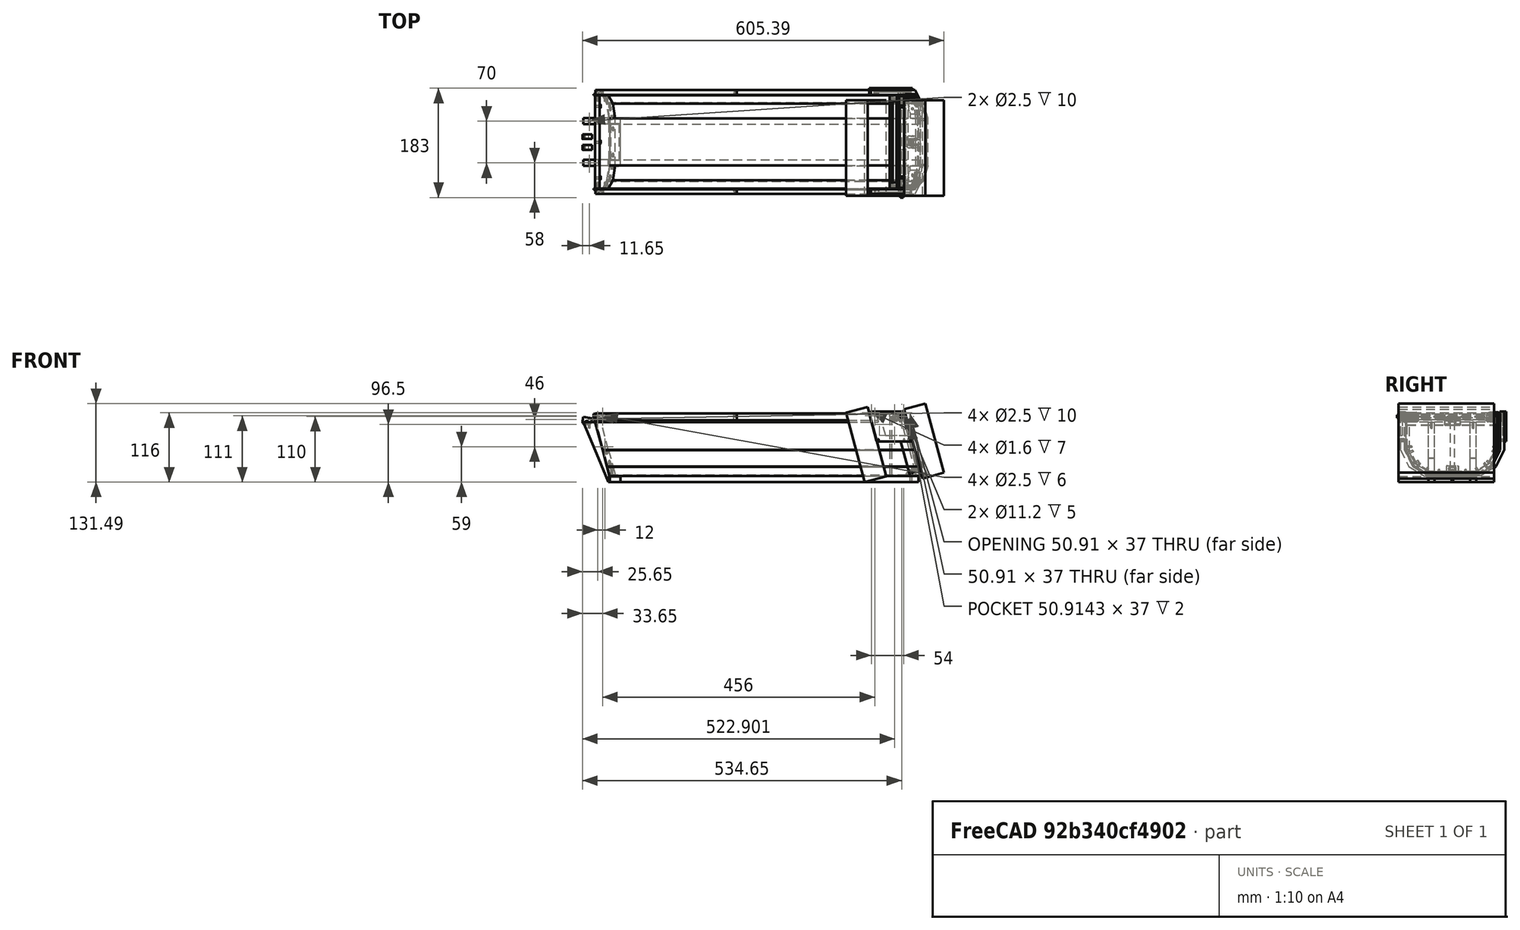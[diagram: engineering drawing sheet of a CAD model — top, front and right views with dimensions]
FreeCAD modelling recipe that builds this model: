
FCSTD DOCUMENT  (FreeCAD 0.16R)
Label: kipper
License: CC-BY 3.0
LicenseURL: http://creativecommons.org/licenses/by/3.0/
objects: Part::Cylinder×116, Part::Box×102, Part::MultiFuse×101, Part::Cut×98, Part::Fillet×19, Part::Extrusion×13, Part::Chamfer×12, Part::Feature×11, Part::Mirroring×6, Sketcher::SketchObject×5, Part::RegularPolygon×1, App::DocumentObjectGroup×1
note: 484 computed .brp shape members not serialized (recipe doc carries the construction recipe); baked Part::Feature solids carry a one-line shape summary decoded from their .brp

FEATURE [Part::Box] Box
  Height = 2
  Length = 560
  Width = 80
FEATURE [Part::Box] Box001
  Height = 2
  Length = 560
  Placement = pos=(0,80,0) rot=(1,0,0;0.541051rad)
  Width = 30
FEATURE [Part::Box] Box002
  Height = 2
  Length = 560
  Placement = pos=(0,106,16) rot=(1,0,0;1.09956rad)
  Width = 31
FEATURE [Part::Box] Box003
  Height = 2
  Length = 560
  Placement = pos=(0,120,44) rot=(1,0,0;1.5708rad)
  Width = 60
FEATURE [Part::Box] Box004
  Height = 2
  Length = 560
  Placement = pos=(0,120,44) rot=(1,0,0;1.5708rad)
  Width = 60
FEATURE [Part::Box] Box005
  Height = 2
  Length = 560
  Placement = pos=(0,106,16) rot=(1,0,0;1.09956rad)
  Width = 31
FEATURE [Part::Box] Box006
  Height = 2
  Length = 560
  Placement = pos=(0,80,0) rot=(1,0,0;0.541051rad)
  Width = 30
FEATURE [Part::Box] Box007  label="Cube"
  Height = 120
  Length = 25
  Placement = pos=(550,-41,0) rot=(0,-1,0;0.261799rad)
  Width = 162
FEATURE [Part::RegularPolygon] RegularPolygon  label="Regular polygon"
  Circumradius = 34.64
  Placement = pos=(0,0,0) rot=(0,-1,0;1.5708rad)
  Polygon = 3
FEATURE [Sketcher::SketchObject] Sketch
  Placement = pos=(0,0,0) rot=(0.57735,0.57735,0.57735;2.0944rad)
  sketch-geometry (4):
    g0: LineSegment StartX=-50 StartY=120 StartZ=0 EndX=130 EndY=120 EndZ=0
    g1: LineSegment StartX=130 StartY=120 StartZ=0 EndX=130 EndY=-10 EndZ=0
    g2: LineSegment StartX=130 StartY=-10 StartZ=0 EndX=-50 EndY=-10 EndZ=0
    g3: LineSegment StartX=-50 StartY=-10 StartZ=0 EndX=-50 EndY=120 EndZ=0
  constraints (8):
    c: Coincident(g0,g1)
    c: Coincident(g1,g2)
    c: Coincident(g2,g3)
    c: Coincident(g3,g0)
    c: Horizontal(g0)
    c: Horizontal(g2)
    c: Vertical(g1)
    c: Vertical(g3)
FEATURE [Part::Feature] Face001
  Placement = pos=(0,0,0) rot=(0,-1,0;0.261799rad)
  shape: bbox 37.01 x 198 x 138.1 mm, 1 faces, 0 solids (baked)
FEATURE [Part::Extrusion] Extrude001
  Base = -> Face001
  Dir = (50,0,0)
  Placement = pos=(-23,0,0) rot=(0,0,1;0rad)
  Solid = false
FEATURE [Sketcher::SketchObject] Sketch001
  Placement = pos=(506,0,0) rot=(0.57735,0.57735,0.57735;2.0944rad)
  sketch-geometry (8):
    g0: LineSegment StartX=-38 StartY=100 StartZ=0 EndX=-38 EndY=44 EndZ=0
    g1: LineSegment StartX=-38 StartY=44 StartZ=0 EndX=-24 EndY=17 EndZ=0
    g2: LineSegment StartX=-24 StartY=17 StartZ=0 EndX=0.5 EndY=2 EndZ=0
    g3: LineSegment StartX=0.5 StartY=2 StartZ=0 EndX=79.5 EndY=2 EndZ=0
    g4: LineSegment StartX=79.5 StartY=2 StartZ=0 EndX=104 EndY=17 EndZ=0
    g5: LineSegment StartX=104 StartY=17 StartZ=0 EndX=118 EndY=44 EndZ=0
    g6: LineSegment StartX=118 StartY=44 StartZ=0 EndX=118 EndY=100 EndZ=0
    g7: LineSegment StartX=118 StartY=100 StartZ=0 EndX=-38 EndY=100 EndZ=0
  constraints (12):
    c: Vertical(g0)
    c: Coincident(g0,g1)
    c: Coincident(g1,g2)
    c: Coincident(g2,g3)
    c: Horizontal(g3)
    c: Coincident(g3,g4)
    c: Coincident(g4,g5)
    c: Coincident(g5,g6)
    c: Vertical(g6)
    c: Coincident(g6,g7)
    c: Coincident(g7,g0)
    c: Horizontal(g7)
FEATURE [Sketcher::SketchObject] Sketch002
  Placement = pos=(0,0,0) rot=(0.57735,0.57735,0.57735;2.0944rad)
  sketch-geometry (8):
    g0: LineSegment StartX=-38 StartY=96.5 StartZ=0 EndX=-38 EndY=38.5 EndZ=0
    g1: LineSegment StartX=-38 StartY=38.5 StartZ=0 EndX=-24 EndY=10.5 EndZ=0
    g2: LineSegment StartX=-24 StartY=10.5 StartZ=0 EndX=0.5 EndY=-5 EndZ=0
    g3: LineSegment StartX=0.5 StartY=-5 StartZ=0 EndX=79.5 EndY=-5 EndZ=0
    g4: LineSegment StartX=79.5 StartY=-5 StartZ=0 EndX=104 EndY=10.5 EndZ=0
    g5: LineSegment StartX=104 StartY=10.5 StartZ=0 EndX=118 EndY=38.5 EndZ=0
    g6: LineSegment StartX=118 StartY=38.5 StartZ=0 EndX=118 EndY=96.5 EndZ=0
    g7: LineSegment StartX=118 StartY=96.5 StartZ=0 EndX=-38 EndY=96.5 EndZ=0
  constraints (12):
    c: Vertical(g0)
    c: Coincident(g0,g1)
    c: Coincident(g1,g2)
    c: Coincident(g2,g3)
    c: Horizontal(g3)
    c: Coincident(g3,g4)
    c: Coincident(g4,g5)
    c: Coincident(g5,g6)
    c: Vertical(g6)
    c: Coincident(g6,g7)
    c: Coincident(g7,g0)
    c: Horizontal(g7)
FEATURE [Part::Feature] Face002
  Placement = pos=(25,0,6.8) rot=(0,-1,0;0.261799rad)
  shape: bbox 28.9 x 171.6 x 107.8 mm, 1 faces, 0 solids (baked)
FEATURE [Part::Extrusion] Extrude002
  Base = -> Face002
  Dir = (10,0,0)
  Solid = false
FEATURE [Part::Box] Box008
  Height = 10
  Length = 517
  Placement = pos=(26.9,0,-10) rot=(0,0,1;0rad)
  Width = 10
FEATURE [Part::Box] Box009
  Height = 45
  Length = 12
  Placement = pos=(25,0,-10) rot=(0,-1,0;0.401426rad)
  Width = 10
FEATURE [Part::Box] Box010
  Height = 67
  Length = 20
  Placement = pos=(8,0,30) rot=(0,-1,0;0.401426rad)
  Width = 10
FEATURE [Part::MultiFuse] Fusion004
  Shapes = -> [Box009,Box010]
FEATURE [Part::Box] Box011
  Height = 10
  Length = 517
  Placement = pos=(26.9,70,-10) rot=(0,0,1;0rad)
  Width = 10
FEATURE [Part::Box] Box012
  Height = 67
  Length = 20
  Placement = pos=(8,0,30) rot=(0,-1,0;0.401426rad)
  Width = 10
FEATURE [Part::Box] Box013
  Height = 45
  Length = 12
  Placement = pos=(25,0,-10) rot=(0,-1,0;0.401426rad)
  Width = 10
FEATURE [Part::MultiFuse] Fusion006
  Placement = pos=(0,70,0) rot=(0,0,1;0rad)
  Shapes = -> [Box013,Box012]
FEATURE [Part::MultiFuse] Fusion007
  Shapes = -> [Fusion004,Fusion006]
FEATURE [Part::Box] Box014
  Height = 15
  Length = 25
  Placement = pos=(-22.3,-38,90) rot=(0,0,1;0rad)
  Width = 156
FEATURE [Part::MultiFuse] Fusion008
  Shapes = -> [Extrude002,Fusion007]
FEATURE [Part::Cut] Cut004
  Base = -> Fusion008
  Tool = -> Box014
FEATURE [Part::Box] Box015
  Height = 10
  Length = 10
  Placement = pos=(25,0,-10) rot=(0,0,1;0rad)
  Width = 10
FEATURE [Part::Box] Box016
  Height = 10
  Length = 10
  Placement = pos=(25,70,-10) rot=(0,0,1;0rad)
  Width = 10
FEATURE [Part::MultiFuse] Fusion009
  Shapes = -> [Cut004,Box015,Box016]
FEATURE [Part::Box] Box017
  Height = 12.2
  Length = 10
  Placement = pos=(26.2,0,-10) rot=(0,0,1;0rad)
  Width = 10
FEATURE [Part::Box] Box018
  Height = 12.2
  Length = 10
  Placement = pos=(26.2,70,-10) rot=(0,0,1;0rad)
  Width = 10
FEATURE [Part::MultiFuse] Fusion010
  Shapes = -> [Box018,Box017]
FEATURE [Part::Cut] Cut005
  Base = -> Fusion009
  Tool = -> Fusion010
FEATURE [Part::Cylinder] Cylinder
  Angle = 360
  Height = 10
  Placement = pos=(-7,5,80) rot=(0,0,1;0rad)
  Radius = 1.25
FEATURE [Part::Cylinder] Cylinder001
  Angle = 360
  Height = 10
  Placement = pos=(-7,75,80) rot=(0,0,1;0rad)
  Radius = 1.25
FEATURE [Part::MultiFuse] Fusion011
  Shapes = -> [Cylinder,Cylinder001]
FEATURE [Part::Cylinder] Cylinder002
  Angle = 360
  Height = 10
  Placement = pos=(2,-20,97) rot=(0,1,0;1.5708rad)
  Radius = 1.6
FEATURE [Part::Cut] Cut006
  Base = -> Cut005
  Tool = -> Fusion011
FEATURE [Part::Cylinder] Cylinder003
  Angle = 360
  Height = 10
  Placement = pos=(2,40,97) rot=(0,1,0;1.5708rad)
  Radius = 1.6
FEATURE [Part::Cylinder] Cylinder004
  Angle = 360
  Height = 10
  Placement = pos=(2,100,97) rot=(0,1,0;1.5708rad)
  Radius = 1.6
FEATURE [Part::Cylinder] Cylinder005
  Angle = 360
  Height = 3
  Placement = pos=(2,-20,97) rot=(0,1,0;1.5708rad)
  Radius = 3.1
FEATURE [Part::Cylinder] Cylinder006
  Angle = 360
  Height = 3
  Placement = pos=(2,40,97) rot=(0,1,0;1.5708rad)
  Radius = 3.1
FEATURE [Part::Cylinder] Cylinder007
  Angle = 360
  Height = 3
  Placement = pos=(2,100,97) rot=(0,1,0;1.5708rad)
  Radius = 3.1
FEATURE [Part::MultiFuse] Fusion012
  Placement = pos=(-1,0,-2) rot=(0,0,1;0rad)
  Shapes = -> [Cylinder002,Cylinder003,Cylinder004]
FEATURE [Part::MultiFuse] Fusion013
  Placement = pos=(8,0,-2) rot=(0,0,1;0rad)
  Shapes = -> [Cylinder005,Cylinder007,Cylinder006]
FEATURE [Part::MultiFuse] Fusion014
  Placement = pos=(-0.8,0,0) rot=(0,0,1;0rad)
  Shapes = -> [Fusion012,Fusion013]
FEATURE [Part::Cut] Cut007
  Base = -> Cut006
  Tool = -> Fusion014
FEATURE [Part::Cylinder] Cylinder008
  Angle = 360
  Height = 10
  Placement = pos=(7,118,95) rot=(1,0,0;1.5708rad)
  Radius = 1.25
FEATURE [Part::Cylinder] Cylinder009
  Angle = 360
  Height = 10
  Placement = pos=(7,-28,95) rot=(1,0,0;1.5708rad)
  Radius = 1.25
FEATURE [Part::Cylinder] Cylinder010
  Angle = 360
  Height = 10
  Placement = pos=(19,118,49) rot=(1,0,0;1.5708rad)
  Radius = 1.25
FEATURE [Part::Cylinder] Cylinder011
  Angle = 360
  Height = 10
  Placement = pos=(19,-28,49) rot=(1,0,0;1.5708rad)
  Radius = 1.25
FEATURE [Part::Cylinder] Cylinder012
  Angle = 360
  Height = 10
  Placement = pos=(26.5,-17,25) rot=(1,0,0;2.02458rad)
  Radius = 1.25
FEATURE [Part::Cylinder] Cylinder013
  Angle = 360
  Height = 10
  Placement = pos=(22,-26,42) rot=(1,0,0;2.02458rad)
  Radius = 1.25
FEATURE [Part::MultiFuse] Fusion015
  Shapes = -> [Cylinder013,Cylinder012]
FEATURE [Part::Cylinder] Cylinder014
  Angle = 360
  Height = 10
  Placement = pos=(22,-26,42) rot=(1,0,0;2.02458rad)
  Radius = 1.25
FEATURE [Part::Cylinder] Cylinder015
  Angle = 360
  Height = 10
  Placement = pos=(26.5,-17,25) rot=(1,0,0;2.02458rad)
  Radius = 1.25
FEATURE [Part::MultiFuse] Fusion016
  Placement = pos=(48.5,133,62.6) rot=(0,1,0;3.14159rad)
  Shapes = -> [Cylinder014,Cylinder015]
FEATURE [Part::Cylinder] Cylinder017
  Angle = 360
  Height = 10
  Placement = pos=(28,-14,22) rot=(1,0,0;2.58309rad)
  Radius = 1.25
FEATURE [Part::Cylinder] Cylinder018
  Angle = 360
  Height = 10
  Placement = pos=(30.5,0,14) rot=(1,0,0;2.58309rad)
  Radius = 1.25
FEATURE [Part::MultiFuse] Fusion017
  Placement = pos=(0,-1,0) rot=(0,0,1;0rad)
  Shapes = -> [Cylinder017,Cylinder018]
FEATURE [Part::Cylinder] Cylinder019
  Angle = 360
  Height = 10
  Placement = pos=(30.5,0,14) rot=(1,0,0;2.58309rad)
  Radius = 1.25
FEATURE [Part::Cylinder] Cylinder020
  Angle = 360
  Height = 10
  Placement = pos=(28,-14,22) rot=(1,0,0;2.58309rad)
  Radius = 1.25
FEATURE [Part::MultiFuse] Fusion018
  Placement = pos=(58.5,99,27.3) rot=(0,1,0;3.14159rad)
  Shapes = -> [Cylinder020,Cylinder019]
FEATURE [Part::Cylinder] Cylinder021
  Angle = 360
  Height = 10
  Placement = pos=(31,18,1) rot=(0,0,1;0rad)
  Radius = 1.25
FEATURE [Part::Cylinder] Cylinder022
  Angle = 360
  Height = 10
  Placement = pos=(31,62,1) rot=(0,0,1;0rad)
  Radius = 1.25
FEATURE [Part::MultiFuse] Fusion019
  Shapes = -> [Cylinder008,Fusion018,Cylinder021,Fusion017,Cylinder009,Fusion015,Cylinder010,Cylinder011,Fusion016,Cylinder022]
FEATURE [Part::Cut] Cut008  label="front-end"
  Base = -> Cut007
  Tool = -> Fusion019
FEATURE [Part::Box] Box019
  Height = 16
  Length = 45
  Placement = pos=(-42.3,-47,90) rot=(0,0,1;0rad)
  Width = 174
FEATURE [Part::Box] Box020
  Height = 10
  Length = 45
  Placement = pos=(-42.3,-37,87) rot=(0,0,1;0rad)
  Width = 37
FEATURE [Part::Box] Box021
  Height = 10
  Length = 45
  Placement = pos=(-42.3,80,87) rot=(0,0,1;0rad)
  Width = 37
FEATURE [Part::Box] Box022
  Height = 10
  Length = 45
  Placement = pos=(-42.3,10,87) rot=(0,0,1;0rad)
  Width = 60
FEATURE [Part::Box] Box023
  Height = 14
  Length = 45
  Placement = pos=(-60.3,-45,83) rot=(0,0,1;0rad)
  Width = 170
FEATURE [Part::Box] Box024
  Height = 11
  Length = 50
  Placement = pos=(-45.3,115,87) rot=(0,1,0;0.15708rad)
  Width = 12
FEATURE [Part::Box] Box025
  Height = 11
  Length = 50
  Placement = pos=(-45.3,-47,87) rot=(0,1,0;0.15708rad)
  Width = 12
FEATURE [Part::Cylinder] Cylinder026
  Angle = 360
  Height = 20
  Placement = pos=(-7,75,89) rot=(0,0,1;0rad)
  Radius = 1.6
FEATURE [Part::Cylinder] Cylinder027
  Angle = 360
  Height = 20
  Placement = pos=(-7,5,89) rot=(0,0,1;0rad)
  Radius = 1.6
FEATURE [Part::Cylinder] Cylinder028
  Angle = 360
  Height = 10
  Placement = pos=(-7,-20,95) rot=(0,1,0;1.5708rad)
  Radius = 1.25
FEATURE [Part::Cylinder] Cylinder029
  Angle = 360
  Height = 10
  Placement = pos=(-7,40,95) rot=(0,1,0;1.5708rad)
  Radius = 1.25
FEATURE [Part::Cylinder] Cylinder030
  Angle = 360
  Height = 10
  Placement = pos=(-7,100,95) rot=(0,1,0;1.5708rad)
  Radius = 1.25
FEATURE [Part::Cylinder] Cylinder031
  Angle = 360
  Height = 3
  Placement = pos=(-7,75,103) rot=(0,0,1;0rad)
  Radius = 3.2
FEATURE [Part::Cylinder] Cylinder032
  Angle = 360
  Height = 3
  Placement = pos=(-7,5,103) rot=(0,0,1;0rad)
  Radius = 3.2
FEATURE [Part::MultiFuse] Fusion024
  Shapes = -> [Cylinder026,Cylinder032,Cylinder031,Cylinder027,Cylinder030,Cylinder028,Cylinder029]
FEATURE [Part::Box] Box026
  Height = 6
  Length = 10
  Placement = pos=(0,-38,100) rot=(0,0,1;0rad)
  Width = 156
FEATURE [Part::Cylinder] Cylinder033
  Angle = 360
  Height = 6
  Placement = pos=(-4.3,-20,95) rot=(0,1,0;1.5708rad)
  Radius = 3
FEATURE [Part::Cylinder] Cylinder034
  Angle = 360
  Height = 10
  Placement = pos=(-7.3,-20,95) rot=(0,1,0;1.5708rad)
  Radius = 1.25
FEATURE [Part::Cut] Cut012
  Base = -> Cylinder033
  Tool = -> Cylinder034
FEATURE [Part::Cylinder] Cylinder035
  Angle = 360
  Height = 10
  Placement = pos=(-7.3,-20,95) rot=(0,1,0;1.5708rad)
  Radius = 1.25
FEATURE [Part::Cylinder] Cylinder036
  Angle = 360
  Height = 6
  Placement = pos=(-4.3,-20,95) rot=(0,1,0;1.5708rad)
  Radius = 3
FEATURE [Part::Cut] Cut013
  Base = -> Cylinder036
  Placement = pos=(0,60,0) rot=(0,0,1;0rad)
  Tool = -> Cylinder035
FEATURE [Part::Cylinder] Cylinder037
  Angle = 360
  Height = 10
  Placement = pos=(-7.3,-20,95) rot=(0,1,0;1.5708rad)
  Radius = 1.25
FEATURE [Part::Cylinder] Cylinder038
  Angle = 360
  Height = 6
  Placement = pos=(-4.3,-20,95) rot=(0,1,0;1.5708rad)
  Radius = 3
FEATURE [Part::Cut] Cut014
  Base = -> Cylinder038
  Placement = pos=(0,120,0) rot=(0,0,1;0rad)
  Tool = -> Cylinder037
FEATURE [Part::MultiFuse] Fusion026
  Shapes = -> [Cut012,Cut014,Cut013]
FEATURE [Part::Feature] Face003
  shape: bbox 2e-07 x 171.6 x 107.8 mm, 1 faces, 0 solids (baked)
FEATURE [Part::Extrusion] Extrude003
  Base = -> Face003
  Dir = (3,0,0)
  Placement = pos=(-10,0,0) rot=(0,0,1;0rad)
  Solid = false
FEATURE [Part::Cylinder] Cylinder039
  Angle = 360
  Height = 10
  Placement = pos=(492,-33,95) rot=(0,1,0;1.5708rad)
  Radius = 1.6
FEATURE [Part::Cylinder] Cylinder040
  Angle = 360
  Height = 10
  Placement = pos=(492,113,95) rot=(0,1,0;1.5708rad)
  Radius = 1.6
FEATURE [Part::MultiFuse] Fusion028
  Shapes = -> [Cylinder039,Cylinder040]
FEATURE [Part::Cut] Cut015
  Base = -> Extrude003
  Tool = -> Fusion028
FEATURE [Part::Cylinder] Cylinder042
  Angle = 360
  Height = 10
  Placement = pos=(499,-33,95) rot=(0,1,0;1.5708rad)
  Radius = 1.2
FEATURE [Part::Box] Box027
  Height = 13
  Length = 13
  Placement = pos=(499,-38,92) rot=(0,0,1;0rad)
  Width = 10
FEATURE [Part::Fillet] Fillet
  Base = -> Box027
  Edges = 2 edges r=3: [Edge2,Edge6]
FEATURE [Part::Fillet] Fillet001
  Base = -> Fillet
  Edges = 1 edges r=1.5: [Edge13]
FEATURE [Part::Box] Box028
  Height = 8
  Length = 3
  Placement = pos=(499,-38,92) rot=(0,0,1;0rad)
  Width = 10
FEATURE [Part::Cylinder] Cylinder043
  Angle = 360
  Height = 156
  Placement = pos=(504,118,100) rot=(1,0,0;1.5708rad)
  Radius = 3.1
FEATURE [Part::Cut] Cut016
  Base = -> Fillet001
  Placement = pos=(-3,0,0) rot=(0,0,1;0rad)
  Tool = -> Box028
FEATURE [Part::Cut] Cut017
  Base = -> Cut016
  Tool = -> Cylinder042
FEATURE [Part::Cylinder] Cylinder044
  Angle = 360
  Height = 156
  Placement = pos=(504,118,100) rot=(1,0,0;1.5708rad)
  Radius = 3.2
FEATURE [Part::Cut] Cut018
  Base = -> Cut017
  Tool = -> Cylinder044
FEATURE [Part::Cylinder] Cylinder045
  Angle = 360
  Height = 156
  Placement = pos=(504,118,100) rot=(1,0,0;1.5708rad)
  Radius = 3.2
FEATURE [Part::Cut] Cut020
  Base = -> Cut016
  Tool = -> Cylinder042
FEATURE [Part::Cut] Cut019
  Base = -> Cut020
  Placement = pos=(0,146,0) rot=(0,0,1;0rad)
  Tool = -> Cylinder045
FEATURE [Part::MultiFuse] Fusion
  Shapes = -> [Box003,Box001,Box002]
FEATURE [Part::MultiFuse] Fusion029
  Shapes = -> [Box004,Box006,Box005]
FEATURE [Part::Mirroring] Part__Mirroring  label="Fusion029 (Mirror #1)"
  Base = (0,0,0)
  Normal = (0,0,1)
  Placement = pos=(0,80,0) rot=(0,0,1;0rad)
  Source = -> Fusion029
FEATURE [Part::MultiFuse] Fusion030
  Shapes = -> [Box,Part__Mirroring,Fusion]
FEATURE [Part::Cut] Cut
  Base = -> Fusion030
  Tool = -> Extrude001
FEATURE [Part::Box] Box029  label="Cube001"
  Height = 100
  Length = 40
  Placement = pos=(510,-41,0) rot=(0,0,1;0rad)
  Width = 162
FEATURE [Part::Box] Box030  label="Cube002"
  Height = 120
  Length = 25
  Placement = pos=(560,-41,0) rot=(0,-1,0;0.459022rad)
  Width = 162
FEATURE [Part::Box] Box031  label="Cube003"
  Height = 100
  Length = 40
  Placement = pos=(520,-41,0) rot=(0,0,1;0rad)
  Width = 162
FEATURE [Part::Box] Box032  label="Cube004"
  Height = 75
  Length = 40
  Placement = pos=(537,-41,55) rot=(0,0,1;0rad)
  Width = 162
FEATURE [Part::Box] Box033  label="Cube005"
  Height = 100
  Length = 40
  Placement = pos=(520,-41,0) rot=(0,0,1;0rad)
  Width = 162
FEATURE [Part::Cut] Cut021
  Base = -> Box029
  Tool = -> Box007
FEATURE [Part::Cut] Cut022
  Base = -> Box031
  Tool = -> Box030
FEATURE [Part::MultiFuse] Fusion031
  Shapes = -> [Cut021,Cut022]
FEATURE [Part::Cut] Cut023
  Base = -> Fusion031
  Tool = -> Box032
FEATURE [Part::Cut] Cut024
  Base = -> Box033
  Tool = -> Cut023
FEATURE [Part::Box] Box034  label="Cube006"
  Height = 100
  Length = 40
  Placement = pos=(520,-41,0) rot=(0,0,1;0rad)
  Width = 162
FEATURE [Part::Cut] Cut027
  Base = -> Fusion031
  Tool = -> Box032
FEATURE [Part::Cut] Cut026
  Base = -> Box034
  Placement = pos=(0,0,1) rot=(0,0,1;0rad)
  Tool = -> Cut027
FEATURE [Part::Feature] Face
  shape: bbox 2e-07 x 176 x 110 mm, 1 faces, 0 solids (baked)
FEATURE [Part::Extrusion] Extrude
  Base = -> Face
  Dir = (60,0,0)
  Solid = false
FEATURE [Part::Box] Box035  label="Cube007"
  Height = 120
  Length = 37
  Placement = pos=(620,-50,-4) rot=(0,-1,0;0.261799rad)
  Width = 160
FEATURE [Part::Feature] Face004
  shape: bbox 2e-07 x 176 x 110 mm, 1 faces, 0 solids (baked)
FEATURE [Part::Box] Box036  label="Cube008"
  Height = 120
  Length = 37.35
  Placement = pos=(562.94,-50,-10) rot=(0,-1,0;0.261799rad)
  Width = 160
FEATURE [Part::Feature] Face005
  shape: bbox 2e-07 x 176 x 110 mm, 1 faces, 0 solids (baked)
FEATURE [Part::Extrusion] Extrude004
  Base = -> Face005
  Dir = (60,0,0)
  Placement = pos=(0,-7,0) rot=(0,0,1;0rad)
  Solid = false
FEATURE [Part::Cut] Cut030
  Base = -> Cut
  Tool = -> Cut024
FEATURE [Part::Feature] Face006
  shape: bbox 2e-07 x 171.6 x 107.8 mm, 1 faces, 0 solids (baked)
FEATURE [Part::Extrusion] Extrude005
  Base = -> Face006
  Dir = (45,0,1)
  Placement = pos=(9,0,0) rot=(0,0,1;0rad)
  Solid = false
FEATURE [Part::Cut] Cut031
  Base = -> Extrude005
  Tool = -> Cut026
FEATURE [Part::Extrusion] Extrude006
  Base = -> Face006
  Dir = (45,0,1)
  Placement = pos=(9,0,0) rot=(0,0,1;0rad)
  Solid = false
FEATURE [Part::Cut] Cut032
  Base = -> Box034
  Placement = pos=(0,0,1) rot=(0,0,1;0rad)
  Tool = -> Cut027
FEATURE [Part::Cut] Cut033
  Base = -> Extrude006
  Placement = pos=(0,2,3) rot=(0,0,1;0rad)
  Tool = -> Cut032
FEATURE [Part::Extrusion] Extrude007
  Base = -> Face006
  Dir = (45,0,1)
  Placement = pos=(9,0,0) rot=(0,0,1;0rad)
  Solid = false
FEATURE [Part::Cut] Cut034
  Base = -> Box034
  Placement = pos=(0,0,1) rot=(0,0,1;0rad)
  Tool = -> Cut027
FEATURE [Part::Cut] Cut035
  Base = -> Extrude007
  Tool = -> Cut034
FEATURE [Part::Cut] Cut036
  Base = -> Cut031
  Tool = -> Cut033
FEATURE [Part::Extrusion] Extrude008
  Base = -> Face006
  Dir = (45,0,1)
  Placement = pos=(9,0,0) rot=(0,0,1;0rad)
  Solid = false
FEATURE [Part::Cut] Cut037
  Base = -> Box034
  Placement = pos=(0,0,1) rot=(0,0,1;0rad)
  Tool = -> Cut027
FEATURE [Part::Cut] Cut038
  Base = -> Extrude008
  Placement = pos=(0,-3,3) rot=(0,0,1;0rad)
  Tool = -> Cut037
FEATURE [Part::Cut] Cut039
  Base = -> Cut035
  Tool = -> Cut038
FEATURE [Part::MultiFuse] Fusion033
  Shapes = -> [Cut036,Cut039]
FEATURE [Part::Box] Box037  label="Cube009"
  Height = 101
  Length = 10
  Placement = pos=(513,-38,0) rot=(0,0,1;0rad)
  Width = 160
FEATURE [Part::Cut] Cut040
  Base = -> Fusion033
  Tool = -> Box037
FEATURE [Part::MultiFuse] Fusion034  label="kipper-frame-METAL"
  Shapes = -> [Box011,Box008]
FEATURE [Part::Box] Box038  label="Cube010"
  Height = 130
  Length = 40
  Placement = pos=(507,-38,-10) rot=(0,-1,0;0.261799rad)
  Width = 160
FEATURE [Part::Cut] Cut041
  Base = -> Cut040
  Tool = -> Box038
FEATURE [Part::Box] Box039  label="Cube011"
  Height = 15
  Length = 4.3
  Placement = pos=(523,-38,85) rot=(0,-1,0;0.261799rad)
  Width = 156
FEATURE [Part::MultiFuse] Fusion035  label="kipper-rear-HOLES"
  Shapes = -> [Box039,Cut041]
FEATURE [Part::Box] Box040  label="Cube012"
  Height = 120
  Length = 80
  Placement = pos=(538.2,-40,44) rot=(0,-1,0;0.261799rad)
  Width = 160
FEATURE [Part::Cut] Cut042  label="kipper-METAL"
  Base = -> Cut030
  Tool = -> Box040
FEATURE [Part::Feature] Face007
  shape: bbox 2e-07 x 171.6 x 107.8 mm, 1 faces, 0 solids (baked)
FEATURE [Part::Extrusion] Extrude009
  Base = -> Face007
  Dir = (50,0,0)
  Placement = pos=(26,0,0) rot=(0,0,1;0rad)
  Solid = false
FEATURE [Part::Box] Box041  label="Cube013"
  Height = 4
  Length = 50
  Placement = pos=(532,-38,100) rot=(0,0,1;0rad)
  Width = 156
FEATURE [Part::MultiFuse] Fusion036
  Shapes = -> [Box041,Extrude009]
FEATURE [Part::Box] Box042  label="Cube014"
  Height = 130
  Length = 40
  Placement = pos=(573,-38,-9) rot=(0,-1,0;0.261799rad)
  Width = 156
FEATURE [Part::Box] Box043  label="Cube015"
  Height = 130
  Length = 30
  Placement = pos=(533.4,-38,-7) rot=(0,-1,0;0.261799rad)
  Width = 156
FEATURE [Part::Cylinder] Cylinder047
  Angle = 360
  Height = 156
  Placement = pos=(518,118,100) rot=(1,0,0;1.5708rad)
  Radius = 4
FEATURE [Part::Cylinder] Cylinder048
  Angle = 360
  Height = 1
  Placement = pos=(518,-37,100) rot=(1,0,0;1.5708rad)
  Radius = 6.5
FEATURE [Part::Cylinder] Cylinder049
  Angle = 360
  Height = 1
  Placement = pos=(518,118,100) rot=(1,0,0;1.5708rad)
  Radius = 6.5
FEATURE [Part::Cylinder] Cylinder050
  Angle = 360
  Height = 4
  Placement = pos=(512.5,-27,99.5) rot=(0,1,0;1.5708rad)
  Radius = 3
FEATURE [Part::Cylinder] Cylinder051
  Angle = 360
  Height = 4
  Placement = pos=(512.5,107,99.5) rot=(0,1,0;1.5708rad)
  Radius = 3
FEATURE [Part::Cylinder] Cylinder052
  Angle = 360
  Height = 5
  Placement = pos=(512.5,-27,99.5) rot=(0,1,0;1.5708rad)
  Radius = 1.25
FEATURE [Part::Cylinder] Cylinder053
  Angle = 360
  Height = 5
  Placement = pos=(512.5,107,99.5) rot=(0,1,0;1.5708rad)
  Radius = 1.25
FEATURE [Sketcher::SketchObject] Sketch003
  Placement = pos=(506,0,0) rot=(0.57735,0.57735,0.57735;2.0944rad)
  sketch-geometry (8):
    g0: LineSegment StartX=-32 StartY=94 StartZ=0 EndX=-32 EndY=44 EndZ=0
    g1: LineSegment StartX=-32 StartY=44 StartZ=0 EndX=-19 EndY=20 EndZ=0
    g2: LineSegment StartX=-19 StartY=20 StartZ=0 EndX=2 EndY=8 EndZ=0
    g3: LineSegment StartX=2 StartY=8 StartZ=0 EndX=79 EndY=8 EndZ=0
    g4: LineSegment StartX=79 StartY=8 StartZ=0 EndX=99 EndY=20 EndZ=0
    g5: LineSegment StartX=99 StartY=20 StartZ=0 EndX=112 EndY=44 EndZ=0
    g6: LineSegment StartX=112 StartY=44 StartZ=0 EndX=112 EndY=94 EndZ=0
    g7: LineSegment StartX=112 StartY=94 StartZ=0 EndX=-32 EndY=94 EndZ=0
  constraints (12):
    c: Vertical(g0)
    c: Coincident(g0,g1)
    c: Coincident(g1,g2)
    c: Coincident(g2,g3)
    c: Horizontal(g3)
    c: Coincident(g3,g4)
    c: Coincident(g4,g5)
    c: Coincident(g5,g6)
    c: Vertical(g6)
    c: Coincident(g6,g7)
    c: Coincident(g7,g0)
    c: Horizontal(g7)
FEATURE [Part::Feature] Face008
  shape: bbox 2e-07 x 158.7 x 95.08 mm, 1 faces, 0 solids (baked)
FEATURE [Part::Box] Box046  label="Cube018"
  Height = 130
  Length = 40
  Placement = pos=(572,-38,1) rot=(0,-1,0;0.261799rad)
  Width = 156
FEATURE [Part::Box] Box047  label="Cube019"
  Height = 130
  Length = 30
  Placement = pos=(538.1,-38,-7) rot=(0,-1,0;0.261799rad)
  Width = 156
FEATURE [Part::MultiFuse] Fusion042
  Placement = pos=(-4,0,-2) rot=(0,0,1;0rad)
  Shapes = -> [Box047,Box046]
FEATURE [Part::Extrusion] Extrude010
  Base = -> Face008
  Dir = (50,0,0)
  Placement = pos=(27,0,0) rot=(0,0,1;0rad)
  Solid = false
FEATURE [Part::Cut] Cut047
  Base = -> Extrude010
  Placement = pos=(-16,0,0) rot=(0,0,1;0rad)
  Tool = -> Fusion042
FEATURE [Part::Box] Box048  label="Cube020"
  Height = 95
  Length = 4
  Placement = pos=(545.64,36,3) rot=(0,-1,0;0.261799rad)
  Width = 8
FEATURE [Part::MultiFuse] Fusion044
  Shapes = -> [Box043,Box042]
FEATURE [Part::Cut] Cut048
  Base = -> Fusion036
  Placement = pos=(-20,0,0) rot=(0,0,1;0rad)
  Tool = -> Fusion044
FEATURE [Part::Cylinder] Cylinder054
  Angle = 360
  Height = 156
  Placement = pos=(518,118,100) rot=(1,0,0;1.5708rad)
  Radius = 2.5
FEATURE [Part::MultiFuse] Fusion045
  Shapes = -> [Cut048,Cylinder047]
FEATURE [Part::MultiFuse] Fusion046
  Shapes = -> [Cylinder050,Cylinder051,Fusion045]
FEATURE [Part::MultiFuse] Fusion047
  Shapes = -> [Cylinder052,Cylinder053]
FEATURE [Part::Cut] Cut049
  Base = -> Fusion046
  Tool = -> Fusion047
FEATURE [Part::Cut] Cut050
  Base = -> Cut049
  Tool = -> Cylinder054
FEATURE [Part::MultiFuse] Fusion048
  Shapes = -> [Cylinder048,Cylinder049]
FEATURE [Part::Cut] Cut051
  Base = -> Cut050
  Tool = -> Fusion048
FEATURE [Part::Cut] Cut052
  Base = -> Cut051
  Tool = -> Cut047
FEATURE [Part::MultiFuse] Fusion049  label="kipper-back-door_"
  Placement = pos=(-2,0,0) rot=(0,0,1;0rad)
  Shapes = -> [Box048,Cut052]
FEATURE [Part::Box] Box049  label="Cube021"
  Height = 15
  Length = 475
  Placement = pos=(0,-40,89) rot=(0,0,1;0rad)
  Width = 8
FEATURE [Part::Cut] Cut053
  Base = -> Extrude004
  Placement = pos=(3,0,0) rot=(0,0,1;0rad)
  Tool = -> Extrude
FEATURE [Part::Cylinder] Cylinder055
  Angle = 360
  Height = 1
  Placement = pos=(518,-37,100) rot=(1,0,0;1.5708rad)
  Radius = 6
FEATURE [Part::Cylinder] Cylinder056
  Angle = 360
  Height = 80
  Placement = pos=(516,27,100) rot=(1,0,0;1.5708rad)
  Radius = 2.5
FEATURE [Part::Cylinder] Cylinder057
  Angle = 360
  Height = 1
  Placement = pos=(518,-37,100) rot=(1,0,0;1.5708rad)
  Radius = 2.5
FEATURE [Part::Cut] Cut055  label="kipper-closure-spacer-METAL"
  Base = -> Cylinder055
  Placement = pos=(-1,0,0) rot=(0,0,1;0rad)
  Tool = -> Cylinder057
FEATURE [Part::Cylinder] Cylinder058
  Angle = 360
  Height = 5
  Placement = pos=(516,-39,100) rot=(1,0,0;1.5708rad)
  Radius = 5.6
FEATURE [Part::Box] Box050  label="Cube022"
  Height = 120
  Length = 47
  Placement = pos=(680,-50,-4) rot=(0,-1,0;0.261799rad)
  Width = 160
FEATURE [Part::Box] Box051  label="Cube023"
  Height = 120
  Length = 37.35
  Placement = pos=(582.94,-50,-10) rot=(0,-1,0;0.261799rad)
  Width = 160
FEATURE [Part::MultiFuse] Fusion050
  Shapes = -> [Box035,Box036]
FEATURE [Part::Box] Box052  label="Cube024"
  Height = 8
  Length = 60
  Placement = pos=(563,-47,100) rot=(0,0,1;0rad)
  Width = 7
FEATURE [Part::MultiFuse] Fusion051
  Shapes = -> [Cut053,Box052]
FEATURE [Part::Cut] Cut056
  Base = -> Fusion051
  Placement = pos=(-69,0,0) rot=(0,0,1;0rad)
  Tool = -> Fusion050
FEATURE [Part::Box] Box054  label="Cube026"
  Height = 50
  Length = 100
  Placement = pos=(566,-47,58) rot=(0,0,1;0rad)
  Width = 7
FEATURE [Part::MultiFuse] Fusion052
  Shapes = -> [Box050,Box051]
FEATURE [Part::Cut] Cut057
  Base = -> Box054
  Placement = pos=(-129,0,0) rot=(0,0,1;0rad)
  Tool = -> Fusion052
FEATURE [Part::Box] Box055  label="Cube027"
  Height = 4
  Length = 100
  Placement = pos=(433,-40,104) rot=(0,0,1;0rad)
  Width = 1
FEATURE [Part::Box] Box056  label="Cube028"
  Height = 120
  Length = 37.35
  Placement = pos=(453.94,-50,-10) rot=(0,-1,0;0.261799rad)
  Width = 160
FEATURE [Part::Box] Box057  label="Cube029"
  Height = 120
  Length = 37
  Placement = pos=(551,-50,-4) rot=(0,-1,0;0.261799rad)
  Width = 160
FEATURE [Part::MultiFuse] Fusion054
  Shapes = -> [Box056,Box057]
FEATURE [Part::Cut] Cut058
  Base = -> Box055
  Tool = -> Fusion054
FEATURE [Part::Box] Box060  label="Cube032"
  Height = 120
  Length = 37.35
  Placement = pos=(470.94,-50,-10) rot=(0,-1,0;0.261799rad)
  Width = 160
FEATURE [Part::Box] Box061  label="Cube033"
  Height = 120
  Length = 37
  Placement = pos=(549,-50,-4) rot=(0,-1,0;0.261799rad)
  Width = 160
FEATURE [Part::Box] Box062  label="Cube034"
  Height = 37
  Length = 64
  Placement = pos=(468,-49,68) rot=(0,0,1;0rad)
  Width = 5
FEATURE [Part::MultiFuse] Fusion056
  Shapes = -> [Box060,Box061]
FEATURE [Part::Cut] Cut059
  Base = -> Box062
  Tool = -> Fusion056
FEATURE [Part::Cylinder] Cylinder059
  Angle = 360
  Height = 9
  Placement = pos=(519.3,-40,106) rot=(1,0,0;1.5708rad)
  Radius = 0.8
FEATURE [Part::Cylinder] Cylinder060
  Angle = 360
  Height = 9
  Placement = pos=(531,-40,61) rot=(1,0,0;1.5708rad)
  Radius = 0.8
FEATURE [Part::Cylinder] Cylinder061
  Angle = 360
  Height = 9
  Placement = pos=(519.3,-40,106) rot=(1,0,0;1.5708rad)
  Radius = 0.8
FEATURE [Part::Cylinder] Cylinder062
  Angle = 360
  Height = 9
  Placement = pos=(531,-40,61) rot=(1,0,0;1.5708rad)
  Radius = 0.8
FEATURE [Sketcher::SketchObject] Sketch004
  Placement = pos=(507,-49,90) rot=(1,0,0;1.5708rad)
  sketch-geometry (4):
    g0: LineSegment StartX=-46 StartY=18 StartZ=0 EndX=-32.6213 EndY=-32 EndZ=0
    g1: LineSegment StartX=-32.6213 StartY=-32 StartZ=0 EndX=27.3934 EndY=-32 EndZ=0
    g2: LineSegment StartX=27.3934 StartY=-32 StartZ=0 EndX=14 EndY=18 EndZ=0
    g3: LineSegment StartX=14 StartY=18 StartZ=0 EndX=-46 EndY=18 EndZ=0
  constraints (6):
    c: Coincident(g0,g1)
    c: Horizontal(g1)
    c: Coincident(g1,g2)
    c: Coincident(g2,g3)
    c: Coincident(g3,g0)
    c: Horizontal(g3)
FEATURE [Part::Box] Box063  label="Cube035"
  Height = 120
  Length = 37.35
  Placement = pos=(453.94,-50,-10) rot=(0,-1,0;0.261799rad)
  Width = 160
FEATURE [Part::Box] Box064  label="Cube036"
  Height = 120
  Length = 37
  Placement = pos=(551,-50,-4) rot=(0,-1,0;0.261799rad)
  Width = 160
FEATURE [Part::Box] Box065  label="Cube037"
  Height = 50
  Length = 76
  Placement = pos=(460,-49,58) rot=(0,0,1;0rad)
  Width = 3
FEATURE [Part::Box] Box066  label="Cube038"
  Height = 120
  Length = 37.35
  Placement = pos=(453.94,-50,-10) rot=(0,-1,0;0.261799rad)
  Width = 160
FEATURE [Part::Box] Box067  label="Cube039"
  Height = 120
  Length = 37
  Placement = pos=(551,-50,-4) rot=(0,-1,0;0.261799rad)
  Width = 160
FEATURE [Part::MultiFuse] Fusion060
  Shapes = -> [Box066,Box067]
FEATURE [Part::Cut] Cut063
  Base = -> Box065
  Placement = pos=(0,-1,0) rot=(0,0,1;0rad)
  Tool = -> Fusion060
FEATURE [Part::MultiFuse] Fusion061
  Shapes = -> [Cylinder060,Cylinder059]
FEATURE [Part::MultiFuse] Fusion063
  Placement = pos=(-54,0,0) rot=(0,0,1;0rad)
  Shapes = -> [Cylinder062,Cylinder061]
FEATURE [Part::MultiFuse] Fusion062
  Placement = pos=(0,-1,0) rot=(0,0,1;0rad)
  Shapes = -> [Fusion063,Fusion061]
FEATURE [Part::Cut] Cut064
  Base = -> Cut063
  Tool = -> Fusion062
FEATURE [Part::Fillet] Fillet007
  Base = -> Cut064
  Edges = 3 edges r=2: [Edge10,Edge11,Edge14]
FEATURE [Part::Chamfer] Chamfer003
  Base = -> Fillet007
  Edges = 1 edges r=3: [Edge20]
FEATURE [Part::Cylinder] Cylinder063
  Angle = 360
  Height = 10
  Placement = pos=(471,-39,101) rot=(1,0,0;1.5708rad)
  Radius = 1.25
FEATURE [Part::Cylinder] Cylinder064
  Angle = 360
  Height = 20
  Placement = pos=(520,-29,61) rot=(1,0,0;1.5708rad)
  Radius = 1.25
FEATURE [Part::Cylinder] Cylinder065
  Angle = 360
  Height = 20
  Placement = pos=(534,-7.3072,22.5449) rot=(1,0,0;2.63545rad)
  Radius = 1.25
FEATURE [Part::MultiFuse] Fusion064
  Shapes = -> [Cylinder063,Cylinder064,Cylinder065]
FEATURE [Part::Box] Box068  label="Cube040"
  Height = 10
  Length = 475
  Placement = pos=(0,-53.1,85.5) rot=(-1,0,0;0.471239rad)
  Width = 10
FEATURE [Part::Box] Box069  label="Cube041"
  Height = 15
  Length = 475
  Placement = pos=(0,-47,90) rot=(0,0,1;0rad)
  Width = 8
FEATURE [Part::Cut] Cut066
  Base = -> Box069
  Tool = -> Box049
FEATURE [Part::Cut] Cut067
  Base = -> Cut066
  Placement = pos=(3,0,0) rot=(0,0,1;0rad)
  Tool = -> Box068
FEATURE [Part::MultiFuse] Fusion067
  Shapes = -> [Box060,Box061]
FEATURE [Part::Box] Box070  label="Cube042"
  Height = 37
  Length = 64
  Placement = pos=(468,-49,68) rot=(0,0,1;0rad)
  Width = 5
FEATURE [Part::Cut] Cut068
  Base = -> Box070
  Tool = -> Fusion067
FEATURE [Part::MultiFuse] Fusion068
  Shapes = -> [Cut056,Cut057,Cut058]
FEATURE [Part::Cut] Cut069
  Base = -> Fusion068
  Tool = -> Cut068
FEATURE [Part::Cut] Cut070
  Base = -> Cut069
  Tool = -> Cylinder058
FEATURE [Part::Cut] Cut071
  Base = -> Cut070
  Tool = -> Fusion064
FEATURE [Part::Cylinder] Cylinder066
  Angle = 360
  Height = 9
  Placement = pos=(531,-40,61) rot=(1,0,0;1.5708rad)
  Radius = 0.8
FEATURE [Part::Cylinder] Cylinder067
  Angle = 360
  Height = 3
  Placement = pos=(519.3,-44,106) rot=(1,0,0;1.5708rad)
  Radius = 2
FEATURE [Part::Cylinder] Cylinder069
  Angle = 360
  Height = 9
  Placement = pos=(519.3,-40,106) rot=(1,0,0;1.5708rad)
  Radius = 0.8
FEATURE [Part::MultiFuse] Fusion069
  Shapes = -> [Cylinder067,Cut071]
FEATURE [Part::Cylinder] Cylinder070
  Angle = 360
  Height = 9
  Placement = pos=(531,-40,61) rot=(1,0,0;1.5708rad)
  Radius = 0.8
FEATURE [Part::Cylinder] Cylinder071
  Angle = 360
  Height = 9
  Placement = pos=(519.3,-40,106) rot=(1,0,0;1.5708rad)
  Radius = 0.8
FEATURE [Part::MultiFuse] Fusion070
  Shapes = -> [Cylinder066,Cylinder069]
FEATURE [Part::MultiFuse] Fusion071
  Placement = pos=(-54,0,0) rot=(0,0,1;0rad)
  Shapes = -> [Cylinder070,Cylinder071]
FEATURE [Part::MultiFuse] Fusion072
  Shapes = -> [Fusion070,Fusion071]
FEATURE [Part::Cut] Cut072
  Base = -> Fusion069
  Tool = -> Fusion072
FEATURE [Part::Cut] Cut073  label="right-back-door-mech-cover_"
  Base = -> Chamfer003
  Tool = -> Cut059
FEATURE [Part::Fillet] Fillet008
  Base = -> Cut072
  Edges = 2 edges r=2: [Edge32,Edge35]
FEATURE [Part::Chamfer] Chamfer  label="right-back-door-mech_"
  Base = -> Fillet008
  Edges = 1 edges r=3: [Edge23]
FEATURE [Part::MultiFuse] Fusion073
  Placement = pos=(0,0,3) rot=(0,0,1;0rad)
  Shapes = -> [Box024,Box025]
FEATURE [Part::MultiFuse] Fusion022
  Placement = pos=(-16,0,0) rot=(0,1,0;0.15708rad)
  Shapes = -> [Box020,Box023,Box022,Box021]
FEATURE [Part::Cut] Cut074
  Base = -> Box019
  Tool = -> Fusion022
FEATURE [Part::Cut] Cut075
  Base = -> Cut074
  Tool = -> Fusion073
FEATURE [Part::MultiFuse] Fusion074
  Shapes = -> [Box026,Cut075]
FEATURE [Part::MultiFuse] Fusion075
  Shapes = -> [Fusion026,Fusion074]
FEATURE [Part::Cut] Cut076
  Base = -> Fusion075
  Tool = -> Fusion024
FEATURE [Part::Box] Box071  label="Cube043"
  Height = 12
  Length = 15
  Placement = pos=(-14,45,86) rot=(0,0,1;0rad)
  Width = 8
FEATURE [Part::Box] Box072  label="Cube044"
  Height = 12
  Length = 15
  Placement = pos=(-14,27,86) rot=(0,0,1;0rad)
  Width = 8
FEATURE [Part::MultiFuse] Fusion076
  Shapes = -> [Box072,Box071]
FEATURE [Part::Fillet] Fillet009
  Base = -> Fusion076
  Edges = 2 edges r=5: [Edge4,Edge16]
FEATURE [Part::Fillet] Fillet010
  Base = -> Fillet009
  Edges = 2 edges r=5: [Edge15,Edge30]
FEATURE [Part::Cylinder] Cylinder072
  Angle = 360
  Height = 30
  Placement = pos=(-6.5,55,90) rot=(1,0,0;1.5708rad)
  Radius = 2.6
FEATURE [Part::Cut] Cut077
  Base = -> Fillet010
  Placement = pos=(-19,0,0) rot=(0,1,0;0.15708rad)
  Tool = -> Cylinder072
FEATURE [Part::MultiFuse] Fusion077  label="cab-protection"
  Shapes = -> [Cut077,Cut076]
FEATURE [Part::Chamfer] Chamfer004
  Base = -> Fillet007
  Edges = 1 edges r=3: [Edge20]
FEATURE [Part::Cut] Cut078
  Base = -> Box062
  Tool = -> Fusion056
FEATURE [Part::Cut] Cut079  label="left-back-door-mech-cover"
  Base = -> Chamfer004
  Tool = -> Cut078
FEATURE [Part::Fillet] Fillet011
  Base = -> Cut072
  Edges = 2 edges r=2: [Edge32,Edge35]
FEATURE [Part::Chamfer] Chamfer005  label="left-back-door-mech"
  Base = -> Fillet011
  Edges = 1 edges r=3: [Edge23]
FEATURE [Part::Mirroring] Part__Mirroring001  label="right-back-door-mech"
  Base = (0,0,0)
  Normal = (0,0,1)
  Placement = pos=(0,80,0) rot=(0,0,1;0rad)
  Source = -> Chamfer
FEATURE [Part::Mirroring] Part__Mirroring002  label="right-back-door-mech-cover"
  Base = (0,0,0)
  Normal = (0,0,1)
  Placement = pos=(0,80,0) rot=(0,0,1;0rad)
  Source = -> Cut073
FEATURE [Part::Box] Box073  label="Cube045"
  Height = 120
  Length = 37
  Placement = pos=(502.2,-50,-4) rot=(0,-1,0;0.261799rad)
  Width = 160
FEATURE [Part::Cut] Cut080
  Base = -> Cut067
  Tool = -> Box073
FEATURE [Part::Cut] Cut082
  Base = -> Cut066
  Placement = pos=(3,0,0) rot=(0,0,1;0rad)
  Tool = -> Box068
FEATURE [Part::Box] Box074  label="Cube046"
  Height = 120
  Length = 37
  Placement = pos=(502.2,-50,-4) rot=(0,-1,0;0.261799rad)
  Width = 160
FEATURE [Part::Cut] Cut081
  Base = -> Cut082
  Tool = -> Box074
FEATURE [Part::Box] Box075  label="Cube047"
  Height = 15
  Length = 237
  Placement = pos=(3,-47,90) rot=(0,0,1;0rad)
  Width = 8
FEATURE [Part::Box] Box076  label="Cube048"
  Height = 15
  Length = 238
  Placement = pos=(240,-47,90) rot=(0,0,1;0rad)
  Width = 8
FEATURE [Part::Cut] Cut083
  Base = -> Cut080
  Tool = -> Box075
FEATURE [Part::Cut] Cut084
  Base = -> Cut081
  Tool = -> Box076
FEATURE [Part::Cylinder] Cylinder073
  Angle = 360
  Height = 10
  Placement = pos=(7,-33,95) rot=(1,0,0;1.5708rad)
  Radius = 3.25
FEATURE [Part::Cut] Cut085
  Base = -> Cut084
  Tool = -> Cylinder073
FEATURE [Part::Cylinder] Cylinder074
  Angle = 360
  Height = 6
  Placement = pos=(471,-40,101) rot=(1,0,0;1.5708rad)
  Radius = 1.25
FEATURE [Part::Box] Box077  label="Cube049"
  Height = 9.4
  Length = 4.8
  Placement = pos=(235.2,-42.8,94.2) rot=(0,0,1;0rad)
  Width = 2.8
FEATURE [Part::Box] Box078  label="Cube050"
  Height = 10.2
  Length = 5.1
  Placement = pos=(234.9,-43.1,93.9) rot=(0,0,1;0rad)
  Width = 3.1
FEATURE [Part::Cylinder] Cylinder075
  Angle = 360
  Height = 6
  Placement = pos=(15,-40,101) rot=(1,0,0;1.5708rad)
  Radius = 1.25
FEATURE [Part::Cylinder] Cylinder076
  Angle = 360
  Height = 6
  Placement = pos=(237.5,-40,101) rot=(1,0,0;1.5708rad)
  Radius = 1.6
FEATURE [Part::Cylinder] Cylinder077
  Angle = 360
  Height = 6
  Placement = pos=(237.5,-40,101) rot=(1,0,0;1.5708rad)
  Radius = 1.25
FEATURE [Part::MultiFuse] Fusion082
  Shapes = -> [Cut083,Box077]
FEATURE [Part::MultiFuse] Fusion083
  Shapes = -> [Cylinder074,Cylinder076]
FEATURE [Part::Cut] Cut089  label="right-border-02_"
  Base = -> Fusion082
  Tool = -> Fusion083
FEATURE [Part::Cut] Cut090
  Base = -> Cut085
  Tool = -> Box078
FEATURE [Part::MultiFuse] Fusion084
  Shapes = -> [Cylinder075,Cylinder077]
FEATURE [Part::Cut] Cut091  label="left-border-01__"
  Base = -> Cut090
  Tool = -> Fusion084
FEATURE [Part::Cylinder] Cylinder078
  Angle = 360
  Height = 10
  Placement = pos=(10,-33,95) rot=(1,0,0;1.5708rad)
  Radius = 3.25
FEATURE [Part::Box] Box079  label="Cube051"
  Height = 6.5
  Length = 3
  Placement = pos=(7,-43,91.75) rot=(0,0,1;0rad)
  Width = 10
FEATURE [Part::MultiFuse] Fusion085
  Shapes = -> [Cylinder078,Box079]
FEATURE [Part::Cut] Cut092  label="right-border-01_"
  Base = -> Cut091
  Tool = -> Fusion085
FEATURE [Part::MultiFuse] Fusion086
  Shapes = -> [Cut083,Box077]
FEATURE [Part::MultiFuse] Fusion087
  Shapes = -> [Cylinder074,Cylinder076]
FEATURE [Part::Cut] Cut093  label="left-border-02"
  Base = -> Fusion086
  Tool = -> Fusion087
FEATURE [Part::MultiFuse] Fusion088
  Shapes = -> [Cylinder078,Box079]
FEATURE [Part::Cut] Cut094  label="left-border-01__001"
  Base = -> Cut090
  Tool = -> Fusion084
FEATURE [Part::Cut] Cut095  label="left-border-01"
  Base = -> Cut094
  Tool = -> Fusion088
FEATURE [Part::Mirroring] Part__Mirroring003  label="right-border-02"
  Base = (0,0,0)
  Normal = (0,0,1)
  Placement = pos=(0,80,0) rot=(0,0,1;0rad)
  Source = -> Cut089
FEATURE [Part::Mirroring] Part__Mirroring004  label="right-border-01"
  Base = (0,0,0)
  Normal = (0,0,1)
  Placement = pos=(0,80,0) rot=(0,0,1;0rad)
  Source = -> Cut092
FEATURE [Part::Cylinder] Cylinder080
  Angle = 360
  Height = 20
  Placement = pos=(532,40,-10) rot=(0,0,1;0rad)
  Radius = 1.5
FEATURE [Part::Box] Box080  label="Cube052"
  Height = 15
  Length = 5
  Placement = pos=(536,30,2) rot=(0,-1,0;0.261799rad)
  Width = 20
FEATURE [Part::Box] Box081  label="Cube053"
  Height = 4
  Length = 16
  Placement = pos=(524,30,2) rot=(0,0,1;0rad)
  Width = 20
FEATURE [Part::Box] Box082  label="Cube054"
  Height = 20
  Length = 3
  Placement = pos=(540,28,2) rot=(0,-1,0;0.261799rad)
  Width = 24
FEATURE [Part::Cylinder] Cylinder081
  Angle = 360
  Height = 20
  Placement = pos=(529,40,-10) rot=(0,0,1;0rad)
  Radius = 1.9
FEATURE [Part::Cylinder] Cylinder082
  Angle = 360
  Height = 20
  Placement = pos=(532,35,7.5) rot=(0,1,0;1.309rad)
  Radius = 1.1
FEATURE [Part::Cylinder] Cylinder083
  Angle = 360
  Height = 20
  Placement = pos=(532,45,7.5) rot=(0,1,0;1.309rad)
  Radius = 1.1
FEATURE [Part::MultiFuse] Fusion090
  Placement = pos=(0,0,4) rot=(0,0,1;0rad)
  Shapes = -> [Cylinder083,Cylinder082]
FEATURE [Part::Box] Box083  label="Cube055"
  Height = 10
  Length = 10
  Placement = pos=(510.5,-37,94) rot=(0,0,1;0rad)
  Width = 154
FEATURE [Part::Cylinder] Cylinder084
  Angle = 360
  Height = 12
  Placement = pos=(509.5,107,99.5) rot=(0,1,0;1.5708rad)
  Radius = 1.25
FEATURE [Part::Cylinder] Cylinder085
  Angle = 360
  Height = 12
  Placement = pos=(509.5,-27,99.5) rot=(0,1,0;1.5708rad)
  Radius = 1.25
FEATURE [Part::MultiFuse] Fusion091
  Shapes = -> [Cylinder084,Cylinder085]
FEATURE [Part::Cut] Cut099
  Base = -> Box083
  Tool = -> Fusion091
FEATURE [Part::MultiFuse] Fusion092
  Shapes = -> [Fusion049,Cut099]
FEATURE [Part::Cylinder] Cylinder086
  Angle = 360
  Height = 160
  Placement = pos=(516,120,100) rot=(1,0,0;1.5708rad)
  Radius = 2.6
FEATURE [Part::Cut] Cut100
  Base = -> Fusion092
  Tool = -> Cylinder086
FEATURE [Part::Fillet] Fillet017  label="kipper-back-door__"
  Base = -> Cut100
  Edges = 2 edges r=2: [Edge9,Edge11]
FEATURE [Part::Cylinder] Cylinder087
  Angle = 360
  Height = 10
  Placement = pos=(532,44,7.5) rot=(0,1,0;1.309rad)
  Radius = 0.8
FEATURE [Part::Cylinder] Cylinder088
  Angle = 360
  Height = 10
  Placement = pos=(532,36,7.5) rot=(0,1,0;1.309rad)
  Radius = 0.8
FEATURE [Part::MultiFuse] Fusion093
  Shapes = -> [Cylinder087,Cylinder088]
FEATURE [App::DocumentObjectGroup] Group  label="Deleted"
  Group = -> [Cut018,Cut019,Cylinder043,Cut015,Cylinder080,Fusion093,Sketch003,Cylinder056,Sketch004,Box063,Box064,Face004,RegularPolygon,Sketch,Sketch001,Sketch002]
FEATURE [Part::Box] Box084  label="Cube056"
  Height = 3
  Length = 11
  Placement = pos=(529,34,2) rot=(0,0,1;0rad)
  Width = 12
FEATURE [Part::Cylinder] Cylinder089
  Angle = 360
  Height = 20
  Placement = pos=(532,40,-5) rot=(0,0,1;0rad)
  Radius = 1.9
FEATURE [Part::MultiFuse] Fusion094
  Shapes = -> [Box084,Fillet017]
FEATURE [Part::Chamfer] Chamfer007
  Base = -> Fusion094
  Edges = 1 edges r=10.2: [Edge10]
FEATURE [Part::Fillet] Fillet018
  Base = -> Chamfer007
  Edges = 1 edges r=1.1: [Edge14]
FEATURE [Part::Cut] Cut101  label="rear-door_OLD"
  Base = -> Fillet018
  Tool = -> Cylinder089
FEATURE [Part::MultiFuse] Fusion095
  Shapes = -> [Box081,Box080]
FEATURE [Part::Cut] Cut102
  Base = -> Fusion095
  Tool = -> Fusion090
FEATURE [Part::Cut] Cut103
  Base = -> Cut102
  Tool = -> Box082
FEATURE [Part::Cut] Cut104
  Base = -> Cut103
  Tool = -> Cylinder081
FEATURE [Part::Fillet] Fillet019
  Base = -> Cut104
  Edges = 2 edges r=5: [Edge1,Edge3]
FEATURE [Part::Fillet] Fillet021
  Base = -> Fillet019
  Edges = 1 edges r=3: [Edge7]
FEATURE [Part::Fillet] Fillet022
  Base = -> Fillet021
  Edges = 1 edges r=3: [Edge28]
FEATURE [Part::Fillet] Fillet023  label="rear-door-closure-lock"
  Base = -> Fillet022
  Edges = 2 edges r=1.5: [Edge22,Edge31]
FEATURE [Part::Box] Box085  label="Cube057"
  Height = 130
  Length = 30
  Placement = pos=(538.1,-38,-7) rot=(0,-1,0;0.261799rad)
  Width = 156
FEATURE [Part::Cylinder] Cylinder090
  Angle = 360
  Height = 160
  Placement = pos=(516,120,100) rot=(1,0,0;1.5708rad)
  Radius = 2.6
FEATURE [Part::Box] Box086  label="Cube058"
  Height = 130
  Length = 40
  Placement = pos=(573,-38,-9) rot=(0,-1,0;0.261799rad)
  Width = 156
FEATURE [Part::Cylinder] Cylinder091
  Angle = 360
  Height = 1
  Placement = pos=(518,-37,100) rot=(1,0,0;1.5708rad)
  Radius = 6.5
FEATURE [Part::Feature] Face009
  shape: bbox 2e-07 x 158.7 x 95.08 mm, 1 faces, 0 solids (baked)
FEATURE [Part::Cylinder] Cylinder092
  Angle = 360
  Height = 4
  Placement = pos=(512.5,107,99.5) rot=(0,1,0;1.5708rad)
  Radius = 3
FEATURE [Part::Box] Box088  label="Cube060"
  Height = 3
  Length = 11
  Placement = pos=(529,34,2) rot=(0,0,1;0rad)
  Width = 12
FEATURE [Part::Cylinder] Cylinder094
  Angle = 360
  Height = 1
  Placement = pos=(518,118,100) rot=(1,0,0;1.5708rad)
  Radius = 6.5
FEATURE [Part::Box] Box089  label="Cube061"
  Height = 130
  Length = 40
  Placement = pos=(572,-38,1) rot=(0,-1,0;0.261799rad)
  Width = 156
FEATURE [Part::MultiFuse] Fusion099
  Placement = pos=(-4,0,-2) rot=(0,0,1;0rad)
  Shapes = -> [Box085,Box089]
FEATURE [Part::Box] Box090  label="Cube062"
  Height = 4
  Length = 50
  Placement = pos=(532,-38,100) rot=(0,0,1;0rad)
  Width = 156
FEATURE [Part::Box] Box091  label="Cube063"
  Height = 95
  Length = 4
  Placement = pos=(545.64,36,3) rot=(0,-1,0;0.261799rad)
  Width = 8
FEATURE [Part::Feature] Face010
  shape: bbox 2e-07 x 171.6 x 107.8 mm, 1 faces, 0 solids (baked)
FEATURE [Part::Extrusion] Extrude011
  Base = -> Face010
  Dir = (50,0,0)
  Placement = pos=(26,0,0) rot=(0,0,1;0rad)
  Solid = false
FEATURE [Part::MultiFuse] Fusion098
  Shapes = -> [Box090,Extrude011]
FEATURE [Part::MultiFuse] Fusion103
  Placement = pos=(-2,0,0) rot=(0,0,1;0rad)
  Shapes = -> [Cylinder091,Cylinder094]
FEATURE [Part::Box] Box092  label="Cube064"
  Height = 130
  Length = 30
  Placement = pos=(533.4,-38,-7) rot=(0,-1,0;0.261799rad)
  Width = 156
FEATURE [Part::MultiFuse] Fusion100
  Shapes = -> [Box092,Box086]
FEATURE [Part::Cut] Cut106
  Base = -> Fusion098
  Placement = pos=(-20,0,0) rot=(0,0,1;0rad)
  Tool = -> Fusion100
FEATURE [Part::Cylinder] Cylinder100
  Angle = 360
  Height = 15
  Placement = pos=(516,117,100) rot=(1,0,0;1.5708rad)
  Radius = 2.5
FEATURE [Part::Extrusion] Extrude012
  Base = -> Face009
  Dir = (50,0,0)
  Placement = pos=(27,0,0) rot=(0,0,1;0rad)
  Solid = false
FEATURE [Part::Cut] Cut110
  Base = -> Extrude012
  Placement = pos=(-16,0,0) rot=(0,0,1;0rad)
  Tool = -> Fusion099
FEATURE [Part::Cut] Cut111
  Base = -> Cut106
  Tool = -> Cut110
FEATURE [Part::MultiFuse] Fusion105
  Placement = pos=(-2,0,0) rot=(0,0,1;0rad)
  Shapes = -> [Cut111,Box091]
FEATURE [Part::Cut] Cut112
  Base = -> Fusion105
  Tool = -> Fusion103
FEATURE [Part::Cylinder] Cylinder102
  Angle = 360
  Height = 9
  Placement = pos=(532,35,7.5) rot=(0,1,0;1.309rad)
  Radius = 0.9
FEATURE [Part::Cylinder] Cylinder103
  Angle = 360
  Height = 9
  Placement = pos=(532,45,7.5) rot=(0,1,0;1.309rad)
  Radius = 0.9
FEATURE [Part::MultiFuse] Fusion106
  Placement = pos=(0,0,4) rot=(0,0,1;0rad)
  Shapes = -> [Cylinder103,Cylinder102]
FEATURE [Part::Cylinder] Cylinder104
  Angle = 360
  Height = 9
  Placement = pos=(509,-34,102.5) rot=(0,1,0;1.309rad)
  Radius = 0.9
FEATURE [Part::Cut] Cut113
  Base = -> Cut112
  Tool = -> Fusion106
FEATURE [Part::Box] Box094  label="Cube066"
  Height = 8
  Length = 10
  Placement = pos=(511,-37,99) rot=(0,0,1;0rad)
  Width = 20
FEATURE [Part::Box] Box095  label="Cube067"
  Height = 130
  Length = 40
  Placement = pos=(573,-38,-9) rot=(0,-1,0;0.261799rad)
  Width = 156
FEATURE [Part::Box] Box096  label="Cube068"
  Height = 130
  Length = 30
  Placement = pos=(533.4,-38,-7) rot=(0,-1,0;0.261799rad)
  Width = 156
FEATURE [Part::MultiFuse] Fusion107
  Placement = pos=(-22,0,0) rot=(0,0,1;0rad)
  Shapes = -> [Box096,Box095]
FEATURE [Part::Chamfer] Chamfer008
  Base = -> Box094
  Edges = 1 edges r=4: [Edge12]
FEATURE [Part::Box] Box097  label="Cube069"
  Height = 8
  Length = 10
  Placement = pos=(511,97,99) rot=(0,0,1;0rad)
  Width = 20
FEATURE [Part::Chamfer] Chamfer009
  Base = -> Box097
  Edges = 1 edges r=4: [Edge10]
FEATURE [Part::MultiFuse] Fusion108
  Shapes = -> [Chamfer008,Chamfer009]
FEATURE [Part::Cut] Cut114
  Base = -> Fusion108
  Tool = -> Fusion107
FEATURE [Part::MultiFuse] Fusion109
  Shapes = -> [Cut113,Cut114]
FEATURE [Part::Cylinder] Cylinder106
  Angle = 360
  Height = 15
  Placement = pos=(516,-22,100) rot=(1,0,0;1.5708rad)
  Radius = 2.5
FEATURE [Part::MultiFuse] Fusion110
  Shapes = -> [Cylinder106,Cylinder100]
FEATURE [Part::Cut] Cut115
  Base = -> Fusion109
  Tool = -> Fusion110
FEATURE [Part::Cylinder] Cylinder107
  Angle = 360
  Height = 9
  Placement = pos=(509,-21,102.5) rot=(0,1,0;1.309rad)
  Radius = 0.9
FEATURE [Part::MultiFuse] Fusion111
  Shapes = -> [Cylinder107,Cylinder104]
FEATURE [Part::Cylinder] Cylinder108
  Angle = 360
  Height = 9
  Placement = pos=(509,-34,102.5) rot=(0,1,0;1.309rad)
  Radius = 0.9
FEATURE [Part::Cylinder] Cylinder109
  Angle = 360
  Height = 9
  Placement = pos=(509,-21,102.5) rot=(0,1,0;1.309rad)
  Radius = 0.9
FEATURE [Part::MultiFuse] Fusion112
  Placement = pos=(2,0,-9) rot=(0,0,1;0rad)
  Shapes = -> [Cylinder109,Cylinder108]
FEATURE [Part::MultiFuse] Fusion113
  Shapes = -> [Fusion112,Fusion111]
FEATURE [Part::Cylinder] Cylinder110
  Angle = 360
  Height = 9
  Placement = pos=(509,-21,102.5) rot=(0,1,0;1.309rad)
  Radius = 0.9
FEATURE [Part::Cylinder] Cylinder111
  Angle = 360
  Height = 9
  Placement = pos=(509,-34,102.5) rot=(0,1,0;1.309rad)
  Radius = 0.9
FEATURE [Part::Cylinder] Cylinder112
  Angle = 360
  Height = 9
  Placement = pos=(509,-34,102.5) rot=(0,1,0;1.309rad)
  Radius = 0.9
FEATURE [Part::Cylinder] Cylinder113
  Angle = 360
  Height = 9
  Placement = pos=(509,-21,102.5) rot=(0,1,0;1.309rad)
  Radius = 0.9
FEATURE [Part::MultiFuse] Fusion114
  Placement = pos=(2,0,-9) rot=(0,0,1;0rad)
  Shapes = -> [Cylinder110,Cylinder111]
FEATURE [Part::MultiFuse] Fusion115
  Shapes = -> [Cylinder113,Cylinder112]
FEATURE [Part::MultiFuse] Fusion116
  Placement = pos=(0,135,0) rot=(0,0,1;0rad)
  Shapes = -> [Fusion114,Fusion115]
FEATURE [Part::MultiFuse] Fusion117
  Shapes = -> [Fusion116,Fusion113]
FEATURE [Part::Cut] Cut116  label="door-rear"
  Base = -> Cut115
  Tool = -> Fusion117
FEATURE [Part::Box] Box098  label="Cube070"
  Height = 130
  Length = 40
  Placement = pos=(569,-38,-9) rot=(0,-1,0;0.261799rad)
  Width = 156
FEATURE [Part::Box] Box099  label="Cube071"
  Height = 130
  Length = 30
  Placement = pos=(533.4,-38,-7) rot=(0,-1,0;0.261799rad)
  Width = 156
FEATURE [Part::MultiFuse] Fusion118
  Placement = pos=(-22,0,0) rot=(0,0,1;0rad)
  Shapes = -> [Box099,Box098]
FEATURE [Part::Box] Box100  label="Cube072"
  Height = 16
  Length = 10
  Placement = pos=(511,-37,98) rot=(0,0,1;0rad)
  Width = 20
FEATURE [Part::Chamfer] Chamfer010
  Base = -> Box100
  Edges = 1 edges r=4: [Edge12]
  Placement = pos=(0,0,-7) rot=(0,0,1;0rad)
FEATURE [Part::Cut] Cut117
  Base = -> Chamfer010
  Placement = pos=(-4,0,0) rot=(0,0,1;0rad)
  Tool = -> Fusion118
FEATURE [Part::Cylinder] Cylinder114
  Angle = 360
  Height = 9
  Placement = pos=(509,-21,102.5) rot=(0,1,0;1.309rad)
  Radius = 0.9
FEATURE [Part::Cylinder] Cylinder115
  Angle = 360
  Height = 9
  Placement = pos=(509,-34,102.5) rot=(0,1,0;1.309rad)
  Radius = 0.9
FEATURE [Part::Cylinder] Cylinder116
  Angle = 360
  Height = 9
  Placement = pos=(509,-34,102.5) rot=(0,1,0;1.309rad)
  Radius = 0.9
FEATURE [Part::Cylinder] Cylinder117
  Angle = 360
  Height = 9
  Placement = pos=(509,-21,102.5) rot=(0,1,0;1.309rad)
  Radius = 0.9
FEATURE [Part::MultiFuse] Fusion119
  Placement = pos=(2,0,-9) rot=(0,0,1;0rad)
  Shapes = -> [Cylinder114,Cylinder115]
FEATURE [Part::MultiFuse] Fusion120
  Shapes = -> [Cylinder117,Cylinder116]
FEATURE [Part::MultiFuse] Fusion121
  Shapes = -> [Fusion119,Fusion120]
FEATURE [Part::Cut] Cut118
  Base = -> Cut117
  Tool = -> Fusion121
FEATURE [Part::Fillet] Fillet024
  Base = -> Cut118
  Edges = 3 edges r=3: [Edge7,Edge15,Edge23]
FEATURE [Part::Chamfer] Chamfer011
  Base = -> Fillet024
  Edges = 2 edges r=1: [Edge7,Edge8]
FEATURE [Part::Cylinder] Cylinder118
  Angle = 360
  Height = 15
  Placement = pos=(516,-22,100) rot=(1,0,0;1.5708rad)
  Radius = 2.4
FEATURE [Part::Cut] Cut119
  Base = -> Chamfer011
  Tool = -> Cylinder118
FEATURE [Part::Cylinder] Cylinder119
  Angle = 360
  Height = 1
  Placement = pos=(509,-34,102.5) rot=(0,1,0;1.309rad)
  Radius = 2
FEATURE [Part::Cylinder] Cylinder120
  Angle = 360
  Height = 1.4
  Placement = pos=(509,-21,102.5) rot=(0,1,0;1.309rad)
  Radius = 2
FEATURE [Part::Cylinder] Cylinder121
  Angle = 360
  Height = 1
  Placement = pos=(509,-21,102.5) rot=(0,1,0;1.309rad)
  Radius = 2
FEATURE [Part::MultiFuse] Fusion122
  Shapes = -> [Cylinder121,Cylinder119]
FEATURE [Part::Cylinder] Cylinder122
  Angle = 360
  Height = 1.4
  Placement = pos=(509,-34,102.5) rot=(0,1,0;1.309rad)
  Radius = 2
FEATURE [Part::MultiFuse] Fusion124
  Placement = pos=(2,0,-9) rot=(0,0,1;0rad)
  Shapes = -> [Cylinder120,Cylinder122]
FEATURE [Part::MultiFuse] Fusion123
  Shapes = -> [Fusion124,Fusion122]
FEATURE [Part::Fillet] Fillet025
  Base = -> Cut119
  Edges = 2 edges r=2: [Edge18,Edge20]
FEATURE [Part::Cut] Cut120  label="door-rear-bar-holder-left"
  Base = -> Fillet025
  Tool = -> Fusion123
FEATURE [Part::Cylinder] Cylinder123
  Angle = 360
  Height = 15
  Placement = pos=(516,-22,100) rot=(1,0,0;1.5708rad)
  Radius = 2.4
FEATURE [Part::Cylinder] Cylinder124
  Angle = 360
  Height = 1
  Placement = pos=(509,-21,102.5) rot=(0,1,0;1.309rad)
  Radius = 2
FEATURE [Part::Cylinder] Cylinder125
  Angle = 360
  Height = 1.4
  Placement = pos=(509,-34,102.5) rot=(0,1,0;1.309rad)
  Radius = 2
FEATURE [Part::Cylinder] Cylinder126
  Angle = 360
  Height = 1.4
  Placement = pos=(509,-21,102.5) rot=(0,1,0;1.309rad)
  Radius = 2
FEATURE [Part::Cylinder] Cylinder127
  Angle = 360
  Height = 1
  Placement = pos=(509,-34,102.5) rot=(0,1,0;1.309rad)
  Radius = 2
FEATURE [Part::Cylinder] Cylinder128
  Angle = 360
  Height = 9
  Placement = pos=(509,-34,102.5) rot=(0,1,0;1.309rad)
  Radius = 0.9
FEATURE [Part::Cylinder] Cylinder129
  Angle = 360
  Height = 9
  Placement = pos=(509,-21,102.5) rot=(0,1,0;1.309rad)
  Radius = 0.9
FEATURE [Part::Box] Box101  label="Cube073"
  Height = 130
  Length = 30
  Placement = pos=(533.4,-38,-7) rot=(0,-1,0;0.261799rad)
  Width = 156
FEATURE [Part::Box] Box102  label="Cube074"
  Height = 16
  Length = 10
  Placement = pos=(511,-37,98) rot=(0,0,1;0rad)
  Width = 20
FEATURE [Part::Chamfer] Chamfer013
  Base = -> Box102
  Edges = 1 edges r=4: [Edge12]
  Placement = pos=(0,0,-7) rot=(0,0,1;0rad)
FEATURE [Part::Box] Box103  label="Cube075"
  Height = 130
  Length = 40
  Placement = pos=(569,-38,-9) rot=(0,-1,0;0.261799rad)
  Width = 156
FEATURE [Part::MultiFuse] Fusion127
  Placement = pos=(-22,0,0) rot=(0,0,1;0rad)
  Shapes = -> [Box101,Box103]
FEATURE [Part::Cut] Cut121
  Base = -> Chamfer013
  Placement = pos=(-4,0,0) rot=(0,0,1;0rad)
  Tool = -> Fusion127
FEATURE [Part::Cylinder] Cylinder130
  Angle = 360
  Height = 9
  Placement = pos=(509,-21,102.5) rot=(0,1,0;1.309rad)
  Radius = 0.9
FEATURE [Part::MultiFuse] Fusion125
  Shapes = -> [Cylinder130,Cylinder128]
FEATURE [Part::Cylinder] Cylinder131
  Angle = 360
  Height = 9
  Placement = pos=(509,-34,102.5) rot=(0,1,0;1.309rad)
  Radius = 0.9
FEATURE [Part::MultiFuse] Fusion128
  Placement = pos=(2,0,-9) rot=(0,0,1;0rad)
  Shapes = -> [Cylinder129,Cylinder131]
FEATURE [Part::MultiFuse] Fusion126
  Shapes = -> [Fusion128,Fusion125]
FEATURE [Part::Cut] Cut122
  Base = -> Cut121
  Tool = -> Fusion126
FEATURE [Part::Fillet] Fillet026
  Base = -> Cut122
  Edges = 3 edges r=3: [Edge7,Edge15,Edge23]
FEATURE [Part::Chamfer] Chamfer012
  Base = -> Fillet026
  Edges = 2 edges r=1: [Edge7,Edge8]
FEATURE [Part::Cut] Cut123
  Base = -> Chamfer012
  Tool = -> Cylinder123
FEATURE [Part::Fillet] Fillet027
  Base = -> Cut123
  Edges = 2 edges r=2: [Edge18,Edge20]
FEATURE [Part::MultiFuse] Fusion130
  Shapes = -> [Cylinder124,Cylinder127]
FEATURE [Part::MultiFuse] Fusion131
  Placement = pos=(2,0,-9) rot=(0,0,1;0rad)
  Shapes = -> [Cylinder126,Cylinder125]
FEATURE [Part::MultiFuse] Fusion129
  Shapes = -> [Fusion131,Fusion130]
FEATURE [Part::Cut] Cut124  label="door-rear-bar-holder-left_"
  Base = -> Fillet027
  Tool = -> Fusion129
FEATURE [Part::Mirroring] Part__Mirroring005  label="door-rear-bar-holder-right"
  Base = (0,0,0)
  Normal = (0,0,1)
  Placement = pos=(0,80,0) rot=(0,0,1;0rad)
  Source = -> Cut124
FEATURE [Part::Box] Box104  label="Cube076"
  Height = 10
  Length = 18
  Placement = pos=(27,0,-10) rot=(0,0,1;0rad)
  Width = 10
FEATURE [Part::Box] Box105  label="Cube077"
  Height = 10
  Length = 18
  Placement = pos=(27,71,-10) rot=(0,0,1;0rad)
  Width = 10
FEATURE [Part::Box] Box106  label="Cube078"
  Height = 2
  Length = 18
  Placement = pos=(27,0,-2) rot=(0,0,1;0rad)
  Width = 81
FEATURE [Part::MultiFuse] Fusion132
  Shapes = -> [Box104,Box106,Box105]
FEATURE [Part::Box] Box107  label="Cube079"
  Height = 10
  Length = 3
  Width = 6
FEATURE [Part::Fillet] Fillet028
  Base = -> Box107
  Edges = 4 edges r=1.49: [Edge1,Edge3,Edge5,Edge7]
  Placement = pos=(31,15.5,-6) rot=(0,0,1;0rad)
FEATURE [Part::Box] Box108  label="Cube080"
  Height = 10
  Length = 3
  Width = 6
FEATURE [Part::Fillet] Fillet029
  Base = -> Box108
  Edges = 4 edges r=1.49: [Edge1,Edge3,Edge5,Edge7]
  Placement = pos=(31,59.5,-6) rot=(0,0,1;0rad)
FEATURE [Part::MultiFuse] Fusion133
  Shapes = -> [Fillet028,Fillet029]
FEATURE [Part::Cut] Cut125
  Base = -> Fusion132
  Tool = -> Fusion133
FEATURE [Part::Chamfer] Chamfer014  label="kipper-frame-missing-part"
  Base = -> Cut125
  Edges = 2 edges r=1.99: [Edge10,Edge14]
  Placement = pos=(0,-0.5,0) rot=(0,0,1;0rad)
